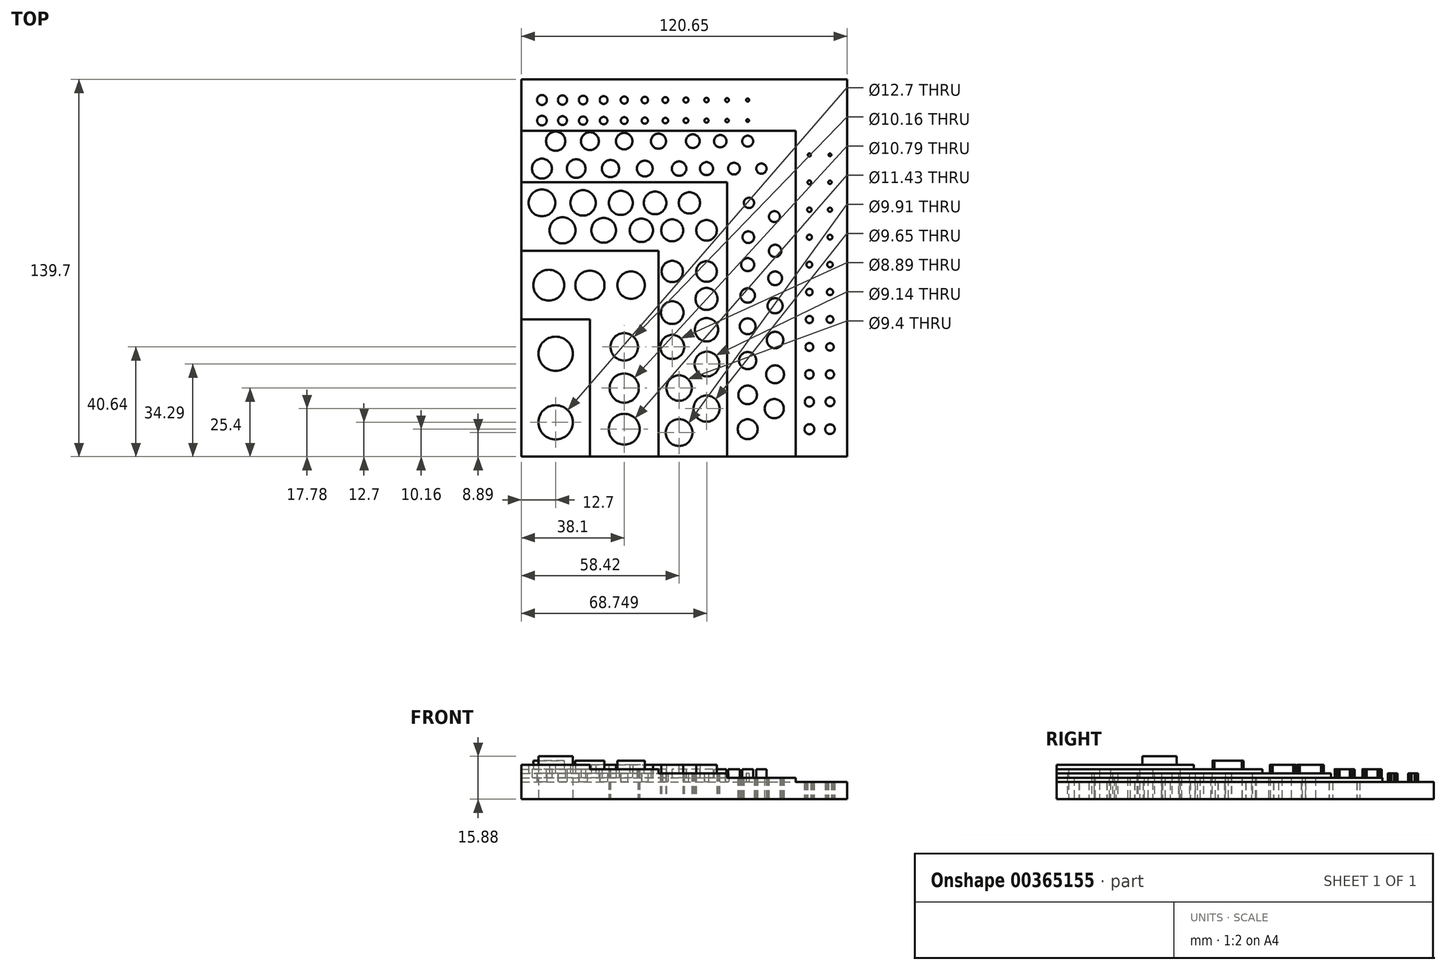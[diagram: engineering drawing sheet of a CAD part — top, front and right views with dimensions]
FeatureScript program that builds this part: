
annotation { "Feature Type Name" : "Feature", "Feature Type Description" : "" }
export const myFeature = defineFeature(function(context is Context, id is Id, definition is map)
    precondition{}
    {
        {
            var Q0;
            Q0=qCreatedBy(makeId("Top.planeOp"),FACE);
            var sketch = newSketch(context, id + "F0", { "sketchPlane" : qUnion([Q0])});
            skLineSegment(sketch, "E0.bottom", {"start": v(0, 0) * mm, "end": v(25.4, 0) * mm});
            skLineSegment(sketch, "E0.top", {"start": v(0, 25.4) * mm, "end": v(25.4, 25.4) * mm});
            skLineSegment(sketch, "E0.left", {"start": v(0, 0) * mm, "end": v(0, 25.4) * mm});
            skLineSegment(sketch, "E0.right", {"start": v(25.4, 0) * mm, "end": v(25.4, 25.4) * mm});
            skSolve(sketch);
        }
        {
            var Q0;
            Q0=makeQuery(id+"F0.imprint","IMPRINT",FACE,{"disambiguationData":[TD([[makeQuery(id+"F0.imprint","IMPRINT",EDGE,{"derivedFrom":sQuery(id+"F0.wireOp",EDGE,"E0.bottom")}),1.0]])]});
            extrude(context, id + "F1", {"entities" : qUnion([Q0]), "depth" : 12.7 * mm});
        }
        {
            var Q0;
            Q0=qCreatedBy(makeId("Top.planeOp"),FACE);
            var sketch = newSketch(context, id + "F2", { "sketchPlane" : qUnion([Q0])});
            skLineSegment(sketch, "E1.bottom", {"start": v(0, 0) * mm, "end": v(25.4, 0) * mm});
            skLineSegment(sketch, "E1.top", {"start": v(0, 50.8) * mm, "end": v(25.4, 50.8) * mm});
            skLineSegment(sketch, "E1.left", {"start": v(0, 0) * mm, "end": v(0, 50.8) * mm});
            skLineSegment(sketch, "E1.right", {"start": v(25.4, 0) * mm, "end": v(25.4, 50.8) * mm});
            skSolve(sketch);
        }
        {
            var Q0;
            Q0 = qSketchRegion(id + "F2", true);
            extrude(context, id + "F3", {"entities" : qUnion([Q0]), "operationType" : NewBodyOperationType.ADD, "depth" : 12.7 * mm});
        }
        {
            var Q0;
            Q0=qCreatedBy(makeId("Top.planeOp"),FACE);
            var sketch = newSketch(context, id + "F4", { "sketchPlane" : qUnion([Q0])});
            skLineSegment(sketch, "E2.bottom", {"start": v(0, 0) * mm, "end": v(50.8, 0) * mm});
            skLineSegment(sketch, "E2.top", {"start": v(0, 50.8) * mm, "end": v(50.8, 50.8) * mm});
            skLineSegment(sketch, "E2.left", {"start": v(0, 0) * mm, "end": v(0, 50.8) * mm});
            skLineSegment(sketch, "E2.right", {"start": v(50.8, 0) * mm, "end": v(50.8, 50.8) * mm});
            skSolve(sketch);
        }
        {
            var Q0;
            Q0 = qSketchRegion(id + "F4", true);
            extrude(context, id + "F5", {"entities" : qUnion([Q0]), "operationType" : NewBodyOperationType.ADD, "depth" : 11.13 * mm});
        }
        {
            var Q0;
            Q0=qCreatedBy(makeId("Top.planeOp"),FACE);
            var sketch = newSketch(context, id + "F6", { "sketchPlane" : qUnion([Q0])});
            skLineSegment(sketch, "E3.bottom", {"start": v(0, 0) * mm, "end": v(50.8, 0) * mm});
            skLineSegment(sketch, "E3.top", {"start": v(0, 76.2) * mm, "end": v(50.8, 76.2) * mm});
            skLineSegment(sketch, "E3.left", {"start": v(0, 0) * mm, "end": v(0, 76.2) * mm});
            skLineSegment(sketch, "E3.right", {"start": v(50.8, 0) * mm, "end": v(50.8, 76.2) * mm});
            skSolve(sketch);
        }
        {
            var Q0;
            Q0 = qSketchRegion(id + "F6", true);
            extrude(context, id + "F7", {"entities" : qUnion([Q0]), "operationType" : NewBodyOperationType.ADD, "depth" : 11.13 * mm});
        }
        {
            var Q0;
            Q0=qCreatedBy(makeId("Top.planeOp"),FACE);
            var sketch = newSketch(context, id + "F8", { "sketchPlane" : qUnion([Q0])});
            skLineSegment(sketch, "E4.bottom", {"start": v(0, 0) * mm, "end": v(76.2, 0) * mm});
            skLineSegment(sketch, "E4.top", {"start": v(0, 76.2) * mm, "end": v(76.2, 76.2) * mm});
            skLineSegment(sketch, "E4.left", {"start": v(0, 0) * mm, "end": v(0, 76.2) * mm});
            skLineSegment(sketch, "E4.right", {"start": v(76.2, 0) * mm, "end": v(76.2, 76.2) * mm});
            skSolve(sketch);
        }
        {
            var Q0;
            Q0 = qSketchRegion(id + "F8", true);
            extrude(context, id + "F9", {"entities" : qUnion([Q0]), "operationType" : NewBodyOperationType.ADD, "depth" : 9.52 * mm});
        }
        {
            var Q0;
            Q0=qCreatedBy(makeId("Top.planeOp"),FACE);
            var sketch = newSketch(context, id + "F10", { "sketchPlane" : qUnion([Q0])});
            skLineSegment(sketch, "E5.bottom", {"start": v(0, 0) * mm, "end": v(76.2, 0) * mm});
            skLineSegment(sketch, "E5.top", {"start": v(0, 101.6) * mm, "end": v(76.2, 101.6) * mm});
            skLineSegment(sketch, "E5.left", {"start": v(0, 0) * mm, "end": v(0, 101.6) * mm});
            skLineSegment(sketch, "E5.right", {"start": v(76.2, 0) * mm, "end": v(76.2, 101.6) * mm});
            skSolve(sketch);
        }
        {
            var Q0;
            Q0 = qSketchRegion(id + "F10", true);
            extrude(context, id + "F11", {"entities" : qUnion([Q0]), "operationType" : NewBodyOperationType.ADD, "depth" : 9.52 * mm});
        }
        {
            var Q0;
            Q0=qCreatedBy(makeId("Top.planeOp"),FACE);
            var sketch = newSketch(context, id + "F12", { "sketchPlane" : qUnion([Q0])});
            skLineSegment(sketch, "E6.bottom", {"start": v(0, 0) * mm, "end": v(101.6, 0) * mm});
            skLineSegment(sketch, "E6.top", {"start": v(0, 101.6) * mm, "end": v(101.6, 101.6) * mm});
            skLineSegment(sketch, "E6.left", {"start": v(0, 0) * mm, "end": v(0, 101.6) * mm});
            skLineSegment(sketch, "E6.right", {"start": v(101.6, 0) * mm, "end": v(101.6, 101.6) * mm});
            skSolve(sketch);
        }
        {
            var Q0;
            Q0 = qSketchRegion(id + "F12", true);
            extrude(context, id + "F13", {"entities" : qUnion([Q0]), "operationType" : NewBodyOperationType.ADD, "depth" : 7.95 * mm});
        }
        {
            var Q0;
            Q0=qCreatedBy(makeId("Top.planeOp"),FACE);
            var sketch = newSketch(context, id + "F14", { "sketchPlane" : qUnion([Q0])});
            skLineSegment(sketch, "E7.bottom", {"start": v(0, 0) * mm, "end": v(101.6, 0) * mm});
            skLineSegment(sketch, "E7.top", {"start": v(0, 120.65) * mm, "end": v(101.6, 120.65) * mm});
            skLineSegment(sketch, "E7.left", {"start": v(0, 0) * mm, "end": v(0, 120.65) * mm});
            skLineSegment(sketch, "E7.right", {"start": v(101.6, 0) * mm, "end": v(101.6, 120.65) * mm});
            skSolve(sketch);
        }
        {
            var Q0;
            Q0 = qSketchRegion(id + "F14", true);
            extrude(context, id + "F15", {"entities" : qUnion([Q0]), "operationType" : NewBodyOperationType.ADD, "depth" : 7.95 * mm});
        }
        {
            var Q0;
            Q0=qCreatedBy(makeId("Top.planeOp"),FACE);
            var sketch = newSketch(context, id + "F16", { "sketchPlane" : qUnion([Q0])});
            skLineSegment(sketch, "E8.bottom", {"start": v(0, 0) * mm, "end": v(120.65, 0) * mm});
            skLineSegment(sketch, "E8.top", {"start": v(0, 120.65) * mm, "end": v(120.65, 120.65) * mm});
            skLineSegment(sketch, "E8.left", {"start": v(0, 0) * mm, "end": v(0, 120.65) * mm});
            skLineSegment(sketch, "E8.right", {"start": v(120.65, 0) * mm, "end": v(120.65, 120.65) * mm});
            skSolve(sketch);
        }
        {
            var Q0;
            Q0 = qSketchRegion(id + "F16", true);
            extrude(context, id + "F17", {"entities" : qUnion([Q0]), "operationType" : NewBodyOperationType.ADD, "depth" : 6.35 * mm});
        }
        {
            var Q0;
            Q0=qCreatedBy(makeId("Top.planeOp"),FACE);
            var sketch = newSketch(context, id + "F18", { "sketchPlane" : qUnion([Q0])});
            skLineSegment(sketch, "E9.bottom", {"start": v(0, 0) * mm, "end": v(120.65, 0) * mm});
            skLineSegment(sketch, "E9.top", {"start": v(0, 139.7) * mm, "end": v(120.65, 139.7) * mm});
            skLineSegment(sketch, "E9.left", {"start": v(0, 0) * mm, "end": v(0, 139.7) * mm});
            skLineSegment(sketch, "E9.right", {"start": v(120.65, 0) * mm, "end": v(120.65, 139.7) * mm});
            skSolve(sketch);
        }
        {
            var Q0;
            Q0 = qSketchRegion(id + "F18", true);
            extrude(context, id + "F19", {"entities" : qUnion([Q0]), "operationType" : NewBodyOperationType.ADD, "depth" : 6.35 * mm});
        }
        {
            var Q0;
            Q0=qCreatedBy(makeId("Top.planeOp"),FACE);
            var sketch = newSketch(context, id + "F20", { "sketchPlane" : qUnion([Q0])});
            skCircle(sketch, "E10", {"center": v(12.7, 12.7) * mm, "radius": 6.35 * mm});
            skSolve(sketch);
        }
        {
            var Q0;
            Q0 = qSketchRegion(id + "F20", true);
            extrude(context, id + "F21", {"entities" : qUnion([Q0]), "operationType" : NewBodyOperationType.REMOVE, "endBound" : BoundingType.THROUGH_ALL, "depth" : 25.4 * mm});
        }
        {
            var Q0;
            Q0=qCreatedBy(makeId("Top.planeOp"),FACE);
            var sketch = newSketch(context, id + "F22", { "sketchPlane" : qUnion([Q0])});
            skCircle(sketch, "E11", {"center": v(12.7, 38.1) * mm, "radius": 6.35 * mm});
            skSolve(sketch);
        }
        {
            var Q0;
            Q0 = qSketchRegion(id + "F22", true);
            var Q1;
            Q1=makeQuery(id+"F1.opExtrude","CAP_FACE",FACE,{"disambiguationData":[OSD([sQuery(id+"F0.wireOp",EDGE,"E0.bottom"),sQuery(id+"F0.wireOp",EDGE,"E0.top"),sQuery(id+"F0.wireOp",EDGE,"E0.left"),sQuery(id+"F0.wireOp",EDGE,"E0.right")])],"isStart":false});
            extrude(context, id + "F23", {"entities" : qUnion([Q0]), "operationType" : NewBodyOperationType.ADD, "endBoundEntityFace" : qUnion([Q1]), "depth" : 15.88 * mm});
        }
        {
            var Q0;
            Q0=qCreatedBy(makeId("Top.planeOp"),FACE);
            var sketch = newSketch(context, id + "F24", { "sketchPlane" : qUnion([Q0])});
            skCircle(sketch, "E12", {"center": v(38.1, 10.16) * mm, "radius": 5.71 * mm});
            skCircle(sketch, "E13", {"center": v(38.1, 25.4) * mm, "radius": 5.4 * mm});
            skCircle(sketch, "E14", {"center": v(38.1, 40.64) * mm, "radius": 5.08 * mm});
            skSolve(sketch);
        }
        {
            var Q0;
            Q0 = qSketchRegion(id + "F24", true);
            extrude(context, id + "F25", {"entities" : qUnion([Q0]), "operationType" : NewBodyOperationType.REMOVE, "endBound" : BoundingType.THROUGH_ALL, "depth" : 25.4 * mm});
        }
        {
            var Q0;
            Q0=qCreatedBy(makeId("Top.planeOp"),FACE);
            var sketch = newSketch(context, id + "F26", { "sketchPlane" : qUnion([Q0])});
            skCircle(sketch, "E15", {"center": v(10.16, 63.5) * mm, "radius": 5.72 * mm});
            skCircle(sketch, "E16", {"center": v(25.4, 63.5) * mm, "radius": 5.4 * mm});
            skCircle(sketch, "E17", {"center": v(40.64, 63.5) * mm, "radius": 5.08 * mm});
            skSolve(sketch);
        }
        {
            var Q0;
            Q0 = qSketchRegion(id + "F26", true);
            var Q1;
            Q1=makeQuery(id+"F3.opExtrude","CAP_FACE",FACE,{"disambiguationData":[OSD([sQuery(id+"F2.wireOp",EDGE,"E1.bottom"),sQuery(id+"F2.wireOp",EDGE,"E1.top"),sQuery(id+"F2.wireOp",EDGE,"E1.left"),sQuery(id+"F2.wireOp",EDGE,"E1.right")])],"isStart":false});
            extrude(context, id + "F27", {"entities" : qUnion([Q0]), "operationType" : NewBodyOperationType.ADD, "endBoundEntityFace" : qUnion([Q1]), "depth" : 14.3 * mm});
        }
        {
            var Q0;
            Q0=qCreatedBy(makeId("Top.planeOp"),FACE);
            var sketch = newSketch(context, id + "F28", { "sketchPlane" : qUnion([Q0])});
            skCircle(sketch, "E18", {"center": v(68.58, 47) * mm, "radius": 4.32 * mm});
            skCircle(sketch, "E19", {"center": v(68.58, 17.78) * mm, "radius": 4.83 * mm});
            skCircle(sketch, "E20", {"center": v(55.88, 53.34) * mm, "radius": 4.2 * mm});
            skCircle(sketch, "E21", {"center": v(68.58, 58.42) * mm, "radius": 4.06 * mm});
            skCircle(sketch, "E22", {"center": v(55.88, 68.58) * mm, "radius": 3.94 * mm});
            skCircle(sketch, "E23", {"center": v(68.58, 68.58) * mm, "radius": 3.81 * mm});
            skCircle(sketch, "E24", {"center": v(58.42, 25.4) * mm, "radius": 4.7 * mm});
            skCircle(sketch, "E25", {"center": v(68.75, 34.3) * mm, "radius": 4.57 * mm});
            skCircle(sketch, "E26", {"center": v(55.88, 40.64) * mm, "radius": 4.45 * mm});
            skCircle(sketch, "E27", {"center": v(58.42, 8.9) * mm, "radius": 4.95 * mm});
            skSolve(sketch);
        }
        {
            var Q0;
            Q0 = qSketchRegion(id + "F28", true);
            extrude(context, id + "F29", {"entities" : qUnion([Q0]), "operationType" : NewBodyOperationType.REMOVE, "endBound" : BoundingType.THROUGH_ALL, "depth" : 25.4 * mm});
        }
        {
            var Q0;
            Q0=qCreatedBy(makeId("Top.planeOp"),FACE);
            var sketch = newSketch(context, id + "F30", { "sketchPlane" : qUnion([Q0])});
            skCircle(sketch, "E28", {"center": v(68.58, 83.82) * mm, "radius": 3.81 * mm});
            skCircle(sketch, "E29", {"center": v(55.88, 83.82) * mm, "radius": 4.06 * mm});
            skCircle(sketch, "E30", {"center": v(62.23, 93.98) * mm, "radius": 3.94 * mm});
            skCircle(sketch, "E31", {"center": v(49.53, 93.98) * mm, "radius": 4.2 * mm});
            skCircle(sketch, "E32", {"center": v(44.45, 83.82) * mm, "radius": 4.32 * mm});
            skCircle(sketch, "E33", {"center": v(36.83, 93.98) * mm, "radius": 4.45 * mm});
            skCircle(sketch, "E34", {"center": v(30.48, 83.82) * mm, "radius": 4.57 * mm});
            skCircle(sketch, "E35", {"center": v(22.86, 93.98) * mm, "radius": 4.7 * mm});
            skCircle(sketch, "E36", {"center": v(15.24, 83.82) * mm, "radius": 4.83 * mm});
            skCircle(sketch, "E37", {"center": v(7.62, 93.98) * mm, "radius": 4.95 * mm});
            skSolve(sketch);
        }
        {
            var Q0;
            Q0 = qSketchRegion(id + "F30", true);
            var Q1;
            Q1=makeQuery(id+"F7.opExtrude","CAP_FACE",FACE,{"disambiguationData":[OSD([sQuery(id+"F6.wireOp",EDGE,"E3.bottom"),sQuery(id+"F6.wireOp",EDGE,"E3.top"),sQuery(id+"F6.wireOp",EDGE,"E3.left"),sQuery(id+"F6.wireOp",EDGE,"E3.right")])],"isStart":false});
            extrude(context, id + "F31", {"entities" : qUnion([Q0]), "operationType" : NewBodyOperationType.ADD, "endBoundEntityFace" : qUnion([Q1]), "depth" : 12.7 * mm});
        }
        {
            var Q0;
            Q0=qCreatedBy(makeId("Top.planeOp"),FACE);
            var sketch = newSketch(context, id + "F32", { "sketchPlane" : qUnion([Q0])});
            skCircle(sketch, "E38", {"center": v(83.82, 10.16) * mm, "radius": 3.68 * mm});
            skCircle(sketch, "E39", {"center": v(93.66, 17.78) * mm, "radius": 3.56 * mm});
            skCircle(sketch, "E40", {"center": v(83.82, 22.86) * mm, "radius": 3.43 * mm});
            skCircle(sketch, "E41", {"center": v(93.98, 43.18) * mm, "radius": 3.05 * mm});
            skCircle(sketch, "E42", {"center": v(83.82, 35.56) * mm, "radius": 3.18 * mm});
            skCircle(sketch, "E43", {"center": v(93.98, 55.88) * mm, "radius": 2.8 * mm});
            skCircle(sketch, "E44", {"center": v(83.82, 59.7) * mm, "radius": 2.67 * mm});
            skCircle(sketch, "E45", {"center": v(93.98, 66.04) * mm, "radius": 2.54 * mm});
            skCircle(sketch, "E46", {"center": v(83.82, 71.12) * mm, "radius": 2.41 * mm});
            skCircle(sketch, "E47", {"center": v(93.98, 76.2) * mm, "radius": 2.29 * mm});
            skCircle(sketch, "E48", {"center": v(93.98, 30.48) * mm, "radius": 3.3 * mm});
            skCircle(sketch, "E49", {"center": v(83.82, 48.26) * mm, "radius": 2.92 * mm});
            skCircle(sketch, "E50", {"center": v(84.07, 81.28) * mm, "radius": 2.16 * mm});
            skCircle(sketch, "E51", {"center": v(93.74, 88.9) * mm, "radius": 2.03 * mm});
            skCircle(sketch, "E52", {"center": v(84.3, 93.98) * mm, "radius": 1.9 * mm});
            skSolve(sketch);
        }
        {
            var Q0;
            Q0 = qSketchRegion(id + "F32", true);
            extrude(context, id + "F33", {"entities" : qUnion([Q0]), "operationType" : NewBodyOperationType.REMOVE, "endBound" : BoundingType.THROUGH_ALL, "depth" : 25.4 * mm});
        }
        {
            var Q0;
            Q0=qCreatedBy(makeId("Top.planeOp"),FACE);
            var sketch = newSketch(context, id + "F34", { "sketchPlane" : qUnion([Q0])});
            skCircle(sketch, "E53", {"center": v(7.62, 106.68) * mm, "radius": 3.68 * mm});
            skCircle(sketch, "E54", {"center": v(12.7, 116.84) * mm, "radius": 3.56 * mm});
            skCircle(sketch, "E55", {"center": v(20.32, 106.68) * mm, "radius": 3.43 * mm});
            skCircle(sketch, "E56", {"center": v(25.4, 116.84) * mm, "radius": 3.3 * mm});
            skCircle(sketch, "E57", {"center": v(38.1, 116.84) * mm, "radius": 3.05 * mm});
            skCircle(sketch, "E58", {"center": v(33.02, 106.68) * mm, "radius": 3.18 * mm});
            skCircle(sketch, "E59", {"center": v(50.8, 116.84) * mm, "radius": 2.8 * mm});
            skCircle(sketch, "E60", {"center": v(45.72, 106.68) * mm, "radius": 2.92 * mm});
            skCircle(sketch, "E61", {"center": v(63.5, 116.84) * mm, "radius": 2.54 * mm});
            skCircle(sketch, "E62", {"center": v(58.42, 106.68) * mm, "radius": 2.67 * mm});
            skCircle(sketch, "E63", {"center": v(73.66, 116.84) * mm, "radius": 2.29 * mm});
            skCircle(sketch, "E64", {"center": v(68.58, 106.68) * mm, "radius": 2.41 * mm});
            skCircle(sketch, "E65", {"center": v(83.82, 116.84) * mm, "radius": 2.03 * mm});
            skCircle(sketch, "E66", {"center": v(78.74, 106.68) * mm, "radius": 2.16 * mm});
            skCircle(sketch, "E67", {"center": v(88.9, 106.68) * mm, "radius": 1.9 * mm});
            skSolve(sketch);
        }
        {
            var Q0;
            Q0 = qSketchRegion(id + "F34", true);
            var Q1;
            Q1=makeQuery(id+"F11.opExtrude","CAP_FACE",FACE,{"disambiguationData":[OSD([sQuery(id+"F10.wireOp",EDGE,"E5.bottom"),sQuery(id+"F10.wireOp",EDGE,"E5.top"),sQuery(id+"F10.wireOp",EDGE,"E5.left"),sQuery(id+"F10.wireOp",EDGE,"E5.right")])],"isStart":false});
            extrude(context, id + "F35", {"entities" : qUnion([Q0]), "operationType" : NewBodyOperationType.ADD, "endBoundEntityFace" : qUnion([Q1]), "depth" : 11.13 * mm});
        }
        {
            var Q0;
            Q0=qCreatedBy(makeId("Top.planeOp"),FACE);
            var sketch = newSketch(context, id + "F36", { "sketchPlane" : qUnion([Q0])});
            skCircle(sketch, "E68", {"center": v(106.68, 10.16) * mm, "radius": 1.84 * mm});
            skCircle(sketch, "E69", {"center": v(114.3, 10.16) * mm, "radius": 1.78 * mm});
            skCircle(sketch, "E70", {"center": v(106.68, 20.32) * mm, "radius": 1.71 * mm});
            skCircle(sketch, "E71", {"center": v(114.3, 20.32) * mm, "radius": 1.65 * mm});
            skCircle(sketch, "E72", {"center": v(106.68, 30.48) * mm, "radius": 1.59 * mm});
            skCircle(sketch, "E73", {"center": v(114.3, 30.48) * mm, "radius": 1.52 * mm});
            skCircle(sketch, "E74", {"center": v(106.68, 40.64) * mm, "radius": 1.46 * mm});
            skCircle(sketch, "E75", {"center": v(114.3, 40.64) * mm, "radius": 1.4 * mm});
            skCircle(sketch, "E76", {"center": v(106.68, 50.8) * mm, "radius": 1.33 * mm});
            skCircle(sketch, "E77", {"center": v(114.3, 50.8) * mm, "radius": 1.27 * mm});
            skCircle(sketch, "E78", {"center": v(106.68, 60.96) * mm, "radius": 1.2 * mm});
            skCircle(sketch, "E79", {"center": v(114.3, 60.96) * mm, "radius": 1.14 * mm});
            skCircle(sketch, "E80", {"center": v(106.68, 71.12) * mm, "radius": 1.08 * mm});
            skCircle(sketch, "E81", {"center": v(114.3, 71.12) * mm, "radius": 1.02 * mm});
            skCircle(sketch, "E82", {"center": v(106.68, 81.28) * mm, "radius": 0.95 * mm});
            skCircle(sketch, "E83", {"center": v(114.3, 81.28) * mm, "radius": 0.89 * mm});
            skCircle(sketch, "E84", {"center": v(106.68, 91.44) * mm, "radius": 0.83 * mm});
            skCircle(sketch, "E85", {"center": v(114.3, 91.44) * mm, "radius": 0.76 * mm});
            skCircle(sketch, "E86", {"center": v(106.68, 101.6) * mm, "radius": 0.7 * mm});
            skCircle(sketch, "E87", {"center": v(114.3, 101.6) * mm, "radius": 0.64 * mm});
            skCircle(sketch, "E88", {"center": v(106.68, 111.76) * mm, "radius": 0.57 * mm});
            skCircle(sketch, "E89", {"center": v(114.3, 111.76) * mm, "radius": 0.5 * mm});
            skSolve(sketch);
        }
        {
            var Q0;
            Q0 = qSketchRegion(id + "F36", true);
            extrude(context, id + "F37", {"entities" : qUnion([Q0]), "operationType" : NewBodyOperationType.REMOVE, "endBound" : BoundingType.THROUGH_ALL, "depth" : 25.4 * mm});
        }
        {
            var Q0;
            Q0=qCreatedBy(makeId("Top.planeOp"),FACE);
            var sketch = newSketch(context, id + "F38", { "sketchPlane" : qUnion([Q0])});
            skCircle(sketch, "E90", {"center": v(7.62, 124.46) * mm, "radius": 1.78 * mm});
            skCircle(sketch, "E91", {"center": v(7.62, 132.08) * mm, "radius": 1.84 * mm});
            skCircle(sketch, "E92", {"center": v(15.24, 132.08) * mm, "radius": 1.71 * mm});
            skCircle(sketch, "E93", {"center": v(15.24, 124.46) * mm, "radius": 1.65 * mm});
            skCircle(sketch, "E94", {"center": v(22.86, 132.08) * mm, "radius": 1.59 * mm});
            skCircle(sketch, "E95", {"center": v(22.86, 124.46) * mm, "radius": 1.52 * mm});
            skCircle(sketch, "E96", {"center": v(30.48, 132.08) * mm, "radius": 1.46 * mm});
            skCircle(sketch, "E97", {"center": v(30.48, 124.46) * mm, "radius": 1.4 * mm});
            skCircle(sketch, "E98", {"center": v(38.1, 132.08) * mm, "radius": 1.33 * mm});
            skCircle(sketch, "E99", {"center": v(38.1, 124.46) * mm, "radius": 1.27 * mm});
            skCircle(sketch, "E100", {"center": v(45.72, 132.08) * mm, "radius": 1.2 * mm});
            skCircle(sketch, "E101", {"center": v(45.72, 124.46) * mm, "radius": 1.14 * mm});
            skCircle(sketch, "E102", {"center": v(53.34, 132.08) * mm, "radius": 1.08 * mm});
            skCircle(sketch, "E103", {"center": v(53.34, 124.46) * mm, "radius": 1.02 * mm});
            skCircle(sketch, "E104", {"center": v(60.96, 132.08) * mm, "radius": 0.95 * mm});
            skCircle(sketch, "E105", {"center": v(60.96, 124.46) * mm, "radius": 0.89 * mm});
            skCircle(sketch, "E106", {"center": v(68.58, 132.08) * mm, "radius": 0.83 * mm});
            skCircle(sketch, "E107", {"center": v(68.58, 124.46) * mm, "radius": 0.76 * mm});
            skCircle(sketch, "E108", {"center": v(76.2, 132.08) * mm, "radius": 0.7 * mm});
            skCircle(sketch, "E109", {"center": v(76.2, 124.46) * mm, "radius": 0.64 * mm});
            skCircle(sketch, "E110", {"center": v(83.82, 132.08) * mm, "radius": 0.57 * mm});
            skCircle(sketch, "E111", {"center": v(83.82, 124.46) * mm, "radius": 0.5 * mm});
            skSolve(sketch);
        }
        {
            var Q0;
            Q0 = qSketchRegion(id + "F38", true);
            var Q1;
            Q1=makeQuery(id+"F17.opExtrude","CAP_FACE",FACE,{"disambiguationData":[OSD([sQuery(id+"F16.wireOp",EDGE,"E8.bottom"),sQuery(id+"F16.wireOp",EDGE,"E8.top"),sQuery(id+"F16.wireOp",EDGE,"E8.left"),sQuery(id+"F16.wireOp",EDGE,"E8.right")])],"isStart":false});
            extrude(context, id + "F39", {"entities" : qUnion([Q0]), "operationType" : NewBodyOperationType.ADD, "endBoundEntityFace" : qUnion([Q1]), "depth" : 9.52 * mm});
        }
    });
